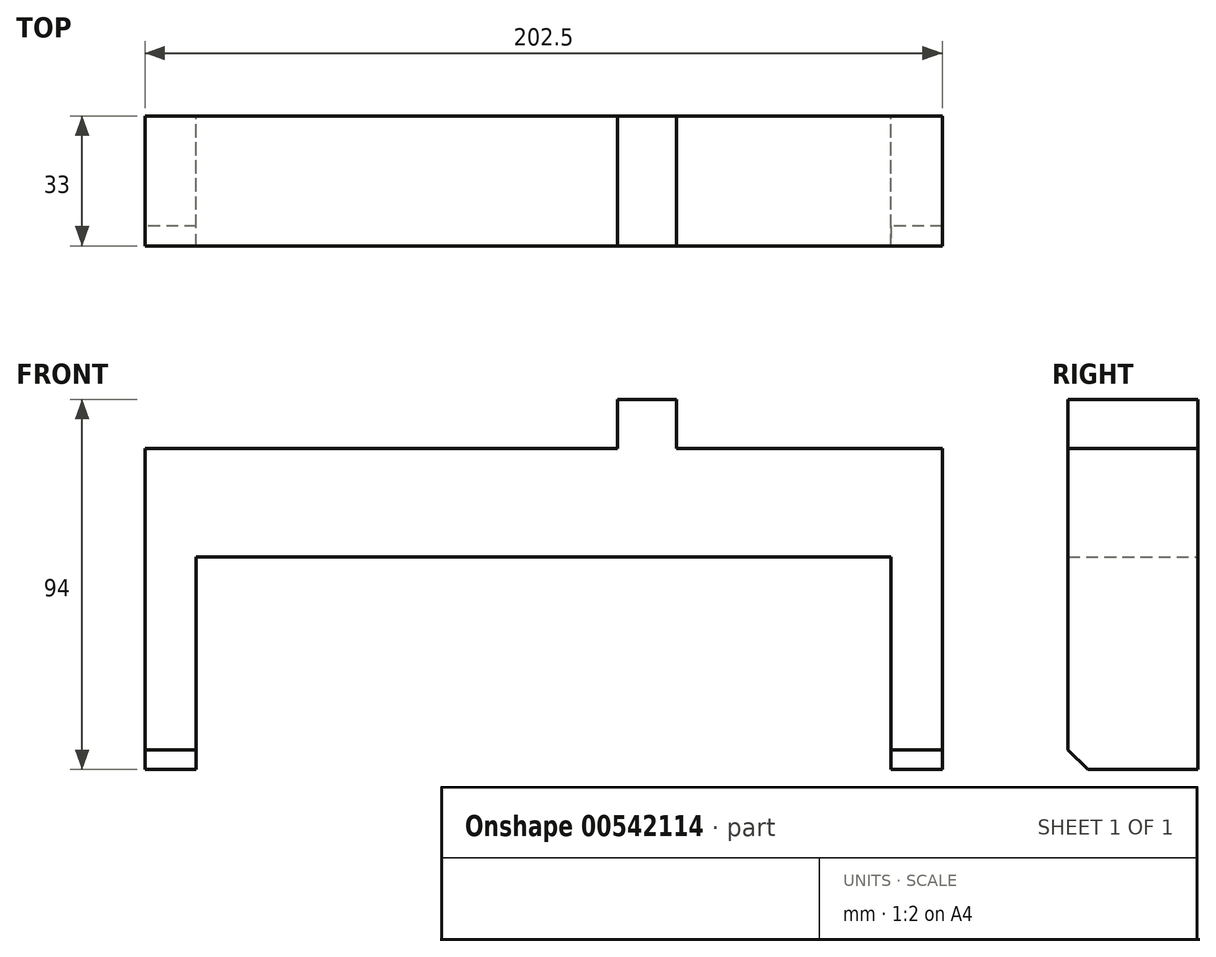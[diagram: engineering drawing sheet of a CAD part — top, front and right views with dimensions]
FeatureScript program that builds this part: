
annotation { "Feature Type Name" : "Feature", "Feature Type Description" : "" }
export const myFeature = defineFeature(function(context is Context, id is Id, definition is map)
    precondition{}
    {
        {
            var Q0;
            Q0=qCreatedBy(makeId("Front.planeOp"),FACE);
            var sketch = newSketch(context, id + "F0", { "sketchPlane" : qUnion([Q0])});
            skLineSegment(sketch, "E0", {"start": v(0, 0) * mm, "end": v(13, 0) * mm});
            skLineSegment(sketch, "E1", {"start": v(13, 0) * mm, "end": v(13, 54) * mm});
            skLineSegment(sketch, "E2", {"start": v(13, 54) * mm, "end": v(189.5, 54) * mm});
            skLineSegment(sketch, "E3", {"start": v(189.5, 54) * mm, "end": v(189.5, 0) * mm});
            skLineSegment(sketch, "E4", {"start": v(189.5, 0) * mm, "end": v(202.5, 0) * mm});
            skLineSegment(sketch, "E5", {"start": v(202.5, 0) * mm, "end": v(202.5, 81.5) * mm});
            skLineSegment(sketch, "E6", {"start": v(202.5, 81.5) * mm, "end": v(135, 81.5) * mm});
            skLineSegment(sketch, "E7", {"start": v(135, 81.5) * mm, "end": v(135, 94) * mm});
            skLineSegment(sketch, "E8", {"start": v(135, 94) * mm, "end": v(120, 94) * mm});
            skLineSegment(sketch, "E9", {"start": v(120, 94) * mm, "end": v(120, 81.5) * mm});
            skLineSegment(sketch, "E10", {"start": v(120, 81.5) * mm, "end": v(0, 81.5) * mm});
            skLineSegment(sketch, "E11", {"start": v(0, 81.5) * mm, "end": v(0, 0) * mm});
            skSolve(sketch);
        }
        {
            var Q0;
            Q0=makeQuery(id+"F0.imprint","IMPRINT",FACE,{"disambiguationData":[TD([[makeQuery(id+"F0.imprint","IMPRINT",EDGE,{"derivedFrom":sQuery(id+"F0.wireOp",EDGE,"E0")}),1.0]])]});
            extrude(context, id + "F1", {"entities" : qUnion([Q0]), "depth" : 33 * mm, "offsetDistance" : 25 * mm});
        }
        {
            var Q0;
            Q0=makeQuery(id+"F1.opExtrude","CAP_EDGE",EDGE,{"disambiguationData":[OSD([sQuery(id+"F0.wireOp",EDGE,"E0")])],"isStart":false});
            chamfer(context, id + "F2", {"entities" : qUnion([Q0]), "width" : 5 * mm, "tangentPropagation" : true});
        }
        {
            var Q0;
            Q0=makeQuery(id+"F1.opExtrude","CAP_EDGE",EDGE,{"disambiguationData":[OSD([sQuery(id+"F0.wireOp",EDGE,"E4")])],"isStart":false});
            chamfer(context, id + "F3", {"entities" : qUnion([Q0]), "width" : 5 * mm, "tangentPropagation" : true});
        }
    });
